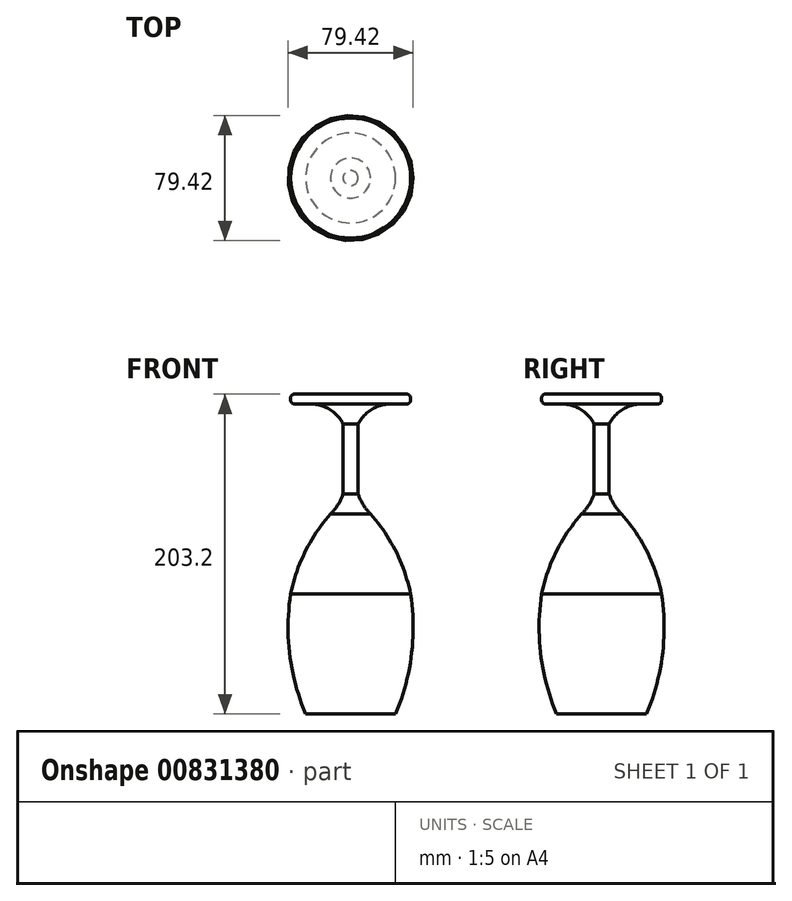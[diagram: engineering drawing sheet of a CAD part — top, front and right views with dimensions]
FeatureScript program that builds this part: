
annotation { "Feature Type Name" : "Feature", "Feature Type Description" : "" }
export const myFeature = defineFeature(function(context is Context, id is Id, definition is map)
    precondition{}
    {
        {
            var Q0;
            Q0=qCreatedBy(makeId("Front.planeOp"),FACE);
            var sketch = newSketch(context, id + "F0", { "sketchPlane" : qUnion([Q0])});
            skLineSegment(sketch, "E0", {"start": v(0, 101.6) * mm, "end": v(0, 0) * mm});
            skLineSegment(sketch, "E1", {"start": v(0, 0) * mm, "end": v(0, -101.6) * mm});
            skLineSegment(sketch, "E2", {"start": v(0, 101.6) * mm, "end": v(-38.1, 101.6) * mm});
            skLineSegment(sketch, "E3", {"start": v(-38.1, 101.6) * mm, "end": v(-38.1, 95.25) * mm});
            skLineSegment(sketch, "E4", {"start": v(0, 82.55) * mm, "end": v(-4.76, 82.55) * mm});
            skLineSegment(sketch, "E5", {"start": v(0, -101.6) * mm, "end": v(-28.57, -101.6) * mm});
            skLineSegment(sketch, "E6", {"start": v(0, -25.4) * mm, "end": v(-38.1, -25.4) * mm});
            skLineSegment(sketch, "E7", {"start": v(0, 25.4) * mm, "end": v(-12.7, 25.4) * mm});
            skLineSegment(sketch, "E8", {"start": v(0, 38.1) * mm, "end": v(-4.76, 38.1) * mm});
            skArc(sketch, "E9", {"start": v(-38.1, -25.4) * mm, "mid": v(-38.62, -64.16) * mm, "end": v(-28.58, -101.6) * mm});
            skArc(sketch, "E10", {"start": v(-12.7, 25.4) * mm, "mid": v(-28.76, 1.68) * mm, "end": v(-38.1, -25.4) * mm});
            skArc(sketch, "E11", {"start": v(-12.7, 25.4) * mm, "mid": v(-8.02, 31.3) * mm, "end": v(-4.76, 38.1) * mm});
            skLineSegment(sketch, "E12", {"start": v(-4.76, 82.55) * mm, "end": v(-4.76, 38.1) * mm});
            skLineSegment(sketch, "E13", {"start": v(-38.1, 95.25) * mm, "end": v(-25.4, 95.25) * mm});
            skArc(sketch, "E14", {"start": v(-4.76, 82.55) * mm, "mid": v(-13.28, 91.82) * mm, "end": v(-25.4, 95.25) * mm});
            skSolve(sketch);
        }
        {
            var Q0;
            Q0 = qSketchRegion(id + "F0", true);
            var Q1;
            Q1=sQuery(id+"F0.wireOp",EDGE,"E0");
            revolve(context, id + "F1", {"surfaceOperationType" : NewSurfaceOperationType.NEW, "entities" : qUnion([Q0]), "axis" : qUnion([Q1]), "revolveType" : RevolveType.FULL});
        }
        {
            var Q0;
            Q0=makeQuery(id+"F1.opRevolve","SWEPT_EDGE",EDGE,{"disambiguationData":[OSD([sQuery(id+"F0.wireOp",EDGE,"E2"),sQuery(id+"F0.wireOp",EDGE,"E3")])]});
            var Q1;
            Q1=makeQuery(id+"F1.opRevolve","SWEPT_EDGE",EDGE,{"disambiguationData":[OSD([sQuery(id+"F0.wireOp",EDGE,"E3"),sQuery(id+"F0.wireOp",EDGE,"E13")])]});
            fillet(context, id + "F2", {"entities" : qUnion([Q0, Q1]), "radius" : 2.54 * mm, "tangentPropagation" : true, "allowEdgeOverflow" : false});
        }
    });
